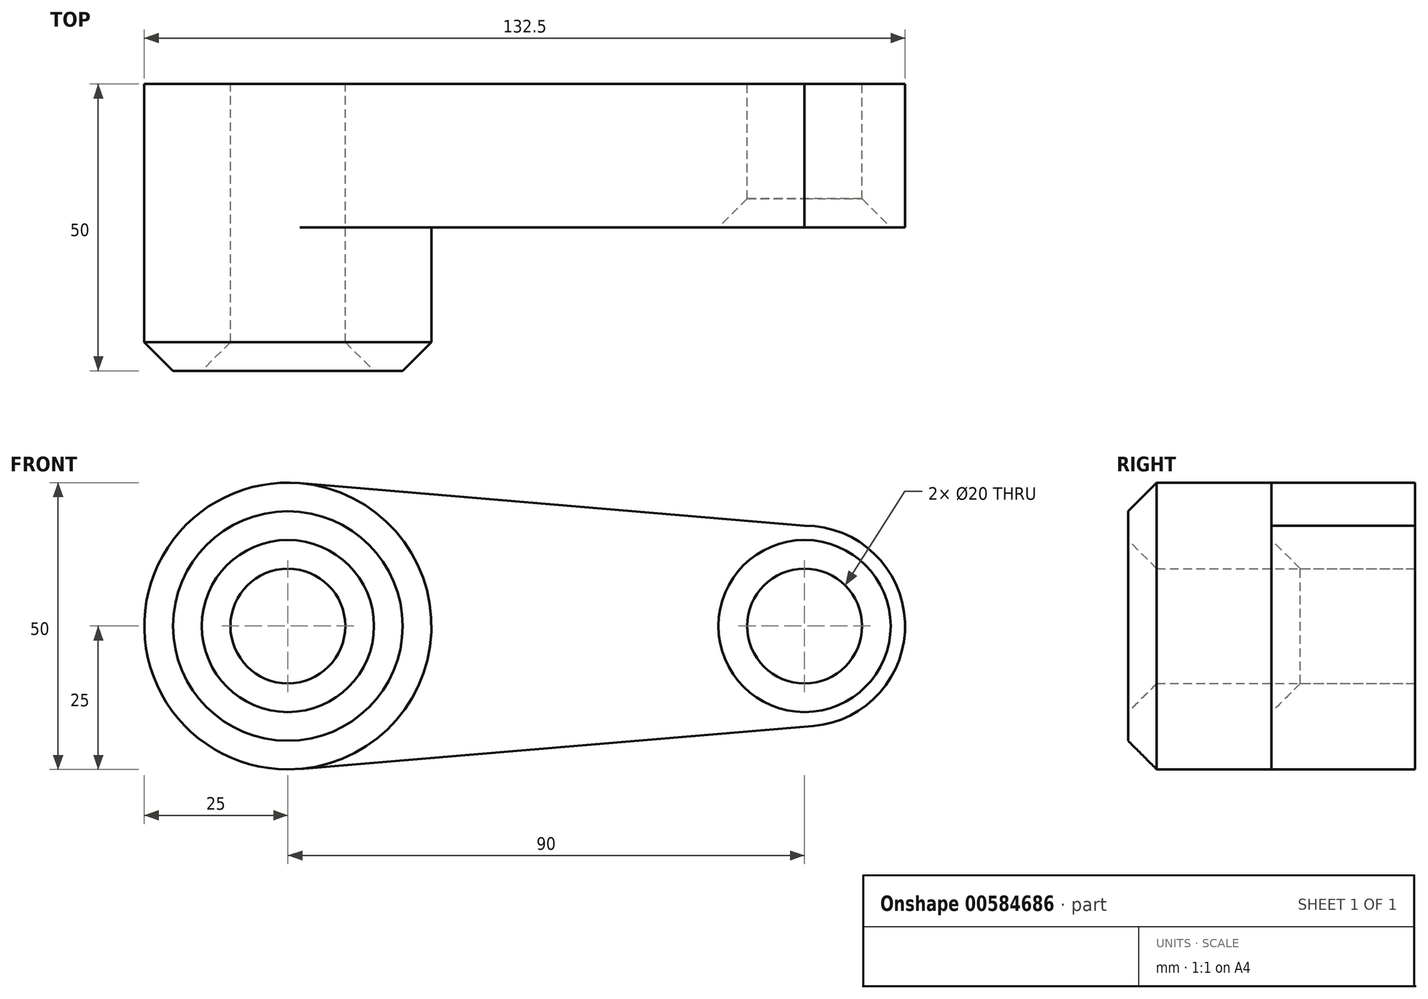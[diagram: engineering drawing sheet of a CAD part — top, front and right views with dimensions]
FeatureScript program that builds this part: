
annotation { "Feature Type Name" : "Feature", "Feature Type Description" : "" }
export const myFeature = defineFeature(function(context is Context, id is Id, definition is map)
    precondition{}
    {
        {
            var Q0;
            Q0=qCreatedBy(makeId("Front.planeOp"),FACE);
            var sketch = newSketch(context, id + "F0", { "sketchPlane" : qUnion([Q0])});
            skCircle(sketch, "E0", {"center": v(0, 0) * mm, "radius": 25 * mm});
            skCircle(sketch, "E1", {"center": v(90, 0) * mm, "radius": 17.5 * mm});
            skLineSegment(sketch, "E2", {"start": v(2.1, 24.91) * mm, "end": v(90, 17.5) * mm});
            skLineSegment(sketch, "E3", {"start": v(2.08, -24.91) * mm, "end": v(91.46, -17.44) * mm});
            skCircle(sketch, "E4", {"center": v(0, 0) * mm, "radius": 10 * mm});
            skCircle(sketch, "E5", {"center": v(90, 0) * mm, "radius": 10 * mm});
            skSolve(sketch);
        }
        {
            var Q0;
            Q0 = qSketchRegion(id + "F0", true);
            extrude(context, id + "F1", {"entities" : qUnion([Q0]), "depth" : 25 * mm, "offsetDistance" : 25 * mm});
        }
        {
            var Q0;
            Q0=makeQuery(id+"F0.imprint","IMPRINT",FACE,{"disambiguationData":[TD([[makeQuery(id+"F0.imprint","IMPRINT",EDGE,{"derivedFrom":sQuery(id+"F0.wireOp",EDGE,"E4")}),-1.0]])]});
            extrude(context, id + "F2", {"entities" : qUnion([Q0]), "operationType" : NewBodyOperationType.ADD, "depth" : 50 * mm, "offsetDistance" : 25 * mm});
        }
        {
            var Q0;
            Q0=makeQuery(id+"F2.opExtrude","CAP_EDGE",EDGE,{"disambiguationData":[OSD([sQuery(id+"F0.wireOp",EDGE,"E0")])],"isStart":false});
            var Q1;
            Q1=makeQuery(id+"F2.opExtrude","CAP_EDGE",EDGE,{"disambiguationData":[OSD([sQuery(id+"F0.wireOp",EDGE,"E4")])],"isStart":false});
            var Q2;
            Q2=makeQuery(id+"F1.opExtrude","CAP_EDGE",EDGE,{"disambiguationData":[OSD([sQuery(id+"F0.wireOp",EDGE,"E5")])],"isStart":false});
            chamfer(context, id + "F3", {"entities" : qUnion([Q0, Q1, Q2]), "width" : 5 * mm, "tangentPropagation" : true});
        }
    });
